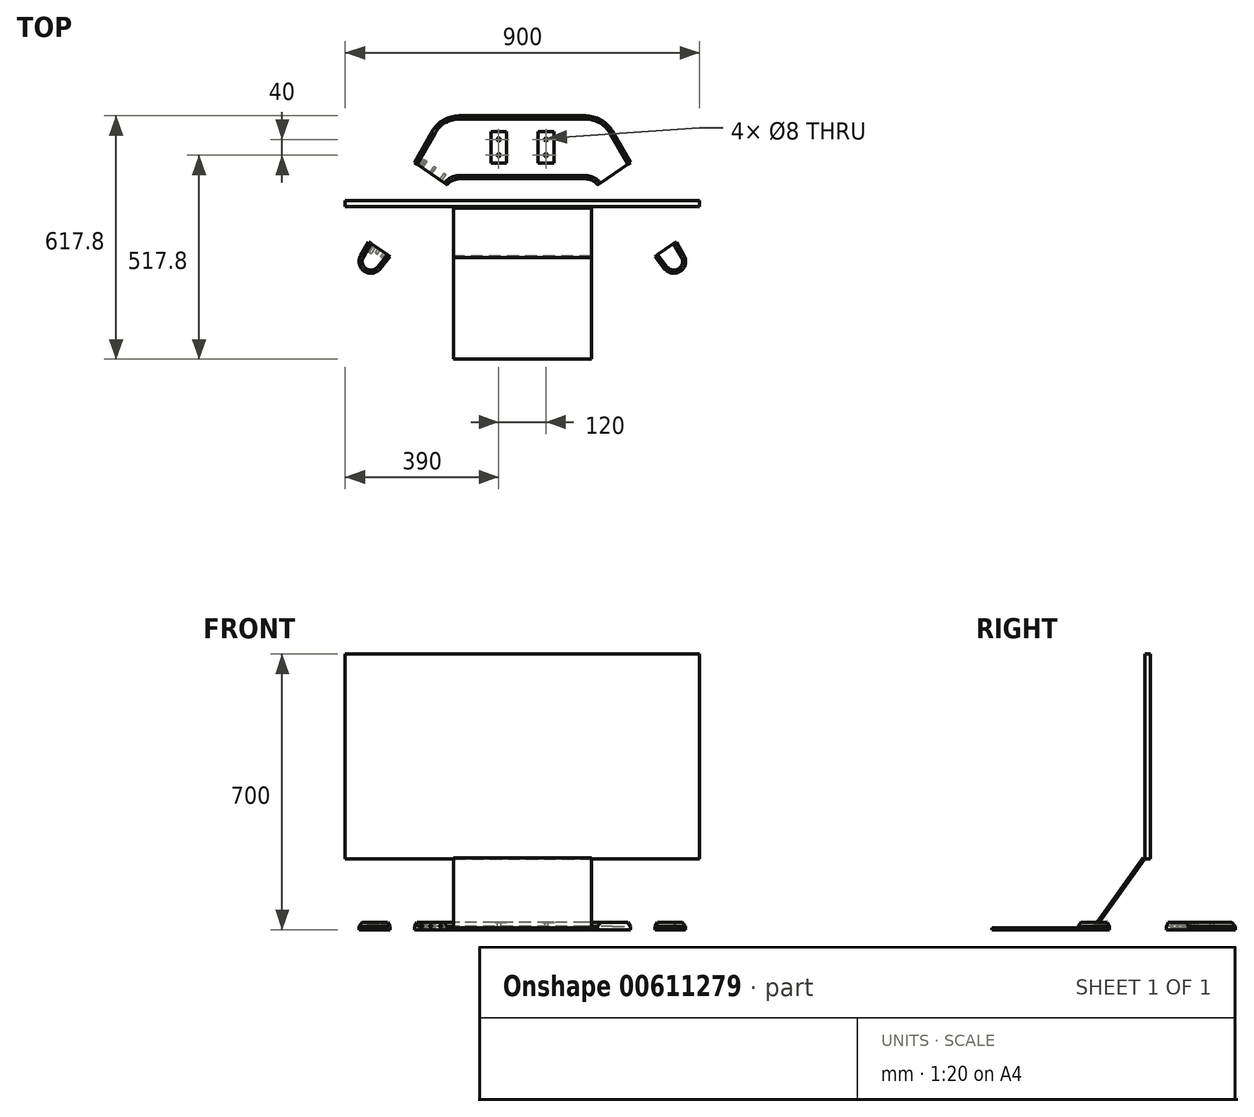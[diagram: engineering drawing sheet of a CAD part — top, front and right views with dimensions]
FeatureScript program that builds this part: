
annotation { "Feature Type Name" : "Feature", "Feature Type Description" : "" }
export const myFeature = defineFeature(function(context is Context, id is Id, definition is map)
    precondition{}
    {
        {
            var Q0;
            Q0=qCreatedBy(makeId("Right.planeOp"),FACE);
            var sketch = newSketch(context, id + "F0", { "sketchPlane" : qUnion([Q0])});
            skLineSegment(sketch, "E0", {"start": v(-150, 180) * mm, "end": v(-150, 700) * mm});
            skLineSegment(sketch, "E1.bottom", {"start": v(-280, 0) * mm, "end": v(-537.8, 0) * mm});
            skLineSegment(sketch, "E1.top", {"start": v(-280, 5) * mm, "end": v(-537.8, 5) * mm});
            skLineSegment(sketch, "E1.left", {"start": v(-280, 0) * mm, "end": v(-280, 5) * mm});
            skLineSegment(sketch, "E1.right", {"start": v(-537.8, 0) * mm, "end": v(-537.8, 5) * mm});
            skLineSegment(sketch, "E2", {"start": v(-280, 5) * mm, "end": v(-275.92, 2.11) * mm});
            skLineSegment(sketch, "E3", {"start": v(-275.92, 2.11) * mm, "end": v(-150, 180) * mm});
            skLineSegment(sketch, "E4", {"start": v(-150, 180) * mm, "end": v(-154.08, 182.89) * mm});
            skLineSegment(sketch, "E5", {"start": v(-154.08, 182.89) * mm, "end": v(-280, 5) * mm});
            skSolve(sketch);
        }
        {
            var Q0;
            Q0=sQuery(id+"F0.wireOp",EDGE,"E0");
            extrude(context, id + "F1", {"bodyType" : ToolBodyType.SURFACE, "surfaceEntities" : qUnion([Q0]), "endBound" : BoundingType.SYMMETRIC, "depth" : 900 * mm, "offsetDistance" : 25 * mm});
        }
        {
            var Q0;
            Q0=makeQuery(id+"F1.opExtrude","SWEPT_FACE",FACE,{"disambiguationData":[OSD([sQuery(id+"F0.wireOp",EDGE,"E0")])]});
            var Q1;
            Q1 = qSketchRegion(id + "FAVnxSPwo9muXU8_0", true);
            extrude(context, id + "F2", {"entities" : qUnion([Q0, Q1]), "depth" : 15 * mm, "offsetDistance" : 25 * mm});
        }
        {
            var Q0;
            Q0=makeQuery(id+"F0.imprint","IMPRINT",FACE,{"disambiguationData":[TD([[makeQuery(id+"F0.imprint","IMPRINT",EDGE,{"derivedFrom":sQuery(id+"F0.wireOp",EDGE,"E2")}),1.0]])]});
            var Q1;
            Q1=makeQuery(id+"F0.imprint","IMPRINT",FACE,{"disambiguationData":[TD([[makeQuery(id+"F0.imprint","IMPRINT",EDGE,{"derivedFrom":sQuery(id+"F0.wireOp",EDGE,"E1.bottom")}),-1.0]])]});
            extrude(context, id + "F3", {"entities" : qUnion([Q0, Q1]), "endBound" : BoundingType.SYMMETRIC, "depth" : 350 * mm, "offsetDistance" : 25 * mm});
        }
        {
            var Q0;
            Q0=qCreatedBy(makeId("Top.planeOp"),FACE);
            var sketch = newSketch(context, id + "F4", { "sketchPlane" : qUnion([Q0])});
            skLineSegment(sketch, "E6.bottom", {"start": v(-40, -40) * mm, "end": v(-80, -40) * mm});
            skLineSegment(sketch, "E6.top", {"start": v(-40, 40) * mm, "end": v(-80, 40) * mm});
            skLineSegment(sketch, "E6.left", {"start": v(-40, -40) * mm, "end": v(-40, 40) * mm});
            skLineSegment(sketch, "E6.right", {"start": v(-80, -40) * mm, "end": v(-80, 40) * mm});
            skPoint(sketch, "E6.middle", {"position": v(-60, 0) * mm});
            skCircle(sketch, "E7", {"center": v(-60, 20) * mm, "radius": 4 * mm});
            skCircle(sketch, "E8", {"center": v(-60, -20) * mm, "radius": 4 * mm});
            skLineSegment(sketch, "E9.bottom", {"start": v(80, -40) * mm, "end": v(40, -40) * mm});
            skLineSegment(sketch, "E9.top", {"start": v(80, 40) * mm, "end": v(40, 40) * mm});
            skLineSegment(sketch, "E9.left", {"start": v(80, -40) * mm, "end": v(80, 40) * mm});
            skLineSegment(sketch, "E9.right", {"start": v(40, -40) * mm, "end": v(40, 40) * mm});
            skPoint(sketch, "E9.middle", {"position": v(60, 0) * mm});
            skCircle(sketch, "E10", {"center": v(60, 20) * mm, "radius": 4 * mm});
            skCircle(sketch, "E11", {"center": v(60, -20) * mm, "radius": 4 * mm});
            skLineSegment(sketch, "E12.bottom", {"start": v(-160, 80) * mm, "end": v(160, 80) * mm});
            skLineSegment(sketch, "E12.top", {"start": v(-160, -80) * mm, "end": v(160, -80) * mm});
            skLineSegment(sketch, "E12.left", {"start": v(-160, 80) * mm, "end": v(-160, -80) * mm});
            skLineSegment(sketch, "E12.right", {"start": v(160, 80) * mm, "end": v(160, -80) * mm});
            skPoint(sketch, "E13", {"position": v(-211.4, -380) * mm});
            skArc(sketch, "E14", {"start": v(-160, 80) * mm, "mid": v(-200.01, 69.27) * mm, "end": v(-229.3, 39.97) * mm});
            skArc(sketch, "E15", {"start": v(-410.99, -275.01) * mm, "mid": v(-401.9, -314.8) * mm, "end": v(-361.54, -308.7) * mm});
            skLineSegment(sketch, "E16", {"start": v(-229.3, 39.97) * mm, "end": v(-410.99, -275.01) * mm});
            skArc(sketch, "E17", {"start": v(-160, -80) * mm, "mid": v(-177.36, -83.96) * mm, "end": v(-191.28, -95.07) * mm});
            skLineSegment(sketch, "E18", {"start": v(-361.54, -308.7) * mm, "end": v(-191.28, -95.07) * mm});
            skArc(sketch, "E19", {"start": v(229.3, 39.97) * mm, "mid": v(200.01, 69.27) * mm, "end": v(160, 80) * mm});
            skArc(sketch, "E20", {"start": v(191.28, -95.07) * mm, "mid": v(177.36, -83.96) * mm, "end": v(160, -80) * mm});
            skArc(sketch, "E21", {"start": v(361.54, -308.7) * mm, "mid": v(401.9, -314.8) * mm, "end": v(410.99, -275.01) * mm});
            skLineSegment(sketch, "E22", {"start": v(191.28, -95.07) * mm, "end": v(361.54, -308.7) * mm});
            skLineSegment(sketch, "E23", {"start": v(229.3, 39.97) * mm, "end": v(410.99, -275.01) * mm});
            skLineSegment(sketch, "E24", {"start": v(-570.65, -290) * mm, "end": v(713.46, -290) * mm, "construction": true});
            skLineSegment(sketch, "E25", {"start": v(0, 249.14) * mm, "end": v(0, -674.1) * mm, "construction": true});
            skLineSegment(sketch, "E26", {"start": v(-390.94, -240.26) * mm, "end": v(-336.54, -277.33) * mm});
            skLineSegment(sketch, "E27", {"start": v(-191.28, -95.07) * mm, "end": v(-274.5, -38.38) * mm});
            skLineSegment(sketch, "E28", {"start": v(-410.99, -275.01) * mm, "end": v(-361.54, -308.7) * mm, "construction": true});
            skLineSegment(sketch, "E29.MirrorCS", {"start": v(191.28, -95.07) * mm, "end": v(274.5, -38.38) * mm});
            skLineSegment(sketch, "E30.MirrorCS", {"start": v(390.94, -240.26) * mm, "end": v(336.54, -277.33) * mm});
            skLineSegment(sketch, "E31", {"start": v(-391.27, -255.77) * mm, "end": v(-350.18, -283.77) * mm});
            skLineSegment(sketch, "E32", {"start": v(-350.18, -283.77) * mm, "end": v(-354.55, -289.26) * mm});
            skLineSegment(sketch, "E33", {"start": v(-354.55, -289.26) * mm, "end": v(-394.78, -261.85) * mm});
            skLineSegment(sketch, "E34", {"start": v(-394.78, -261.85) * mm, "end": v(-391.27, -255.77) * mm});
            skSolve(sketch);
        }
        {
            var Q0;
            Q0=makeQuery(id+"F4.imprint","IMPRINT",FACE,{"disambiguationData":[TD([[makeQuery(id+"F4.imprint","IMPRINT",EDGE,{"derivedFrom":sQuery(id+"F4.wireOp",EDGE,"E6.bottom")}),1.0]])]});
            extrude(context, id + "F5", {"entities" : qUnion([Q0]), "depth" : 18 * mm, "offsetDistance" : 25 * mm});
        }
        {
            var Q0;
            Q0=makeQuery(id+"F4.imprint","IMPRINT",FACE,{"disambiguationData":[TD([[makeQuery(id+"F4.imprint","IMPRINT",EDGE,{"derivedFrom":sQuery(id+"F4.wireOp",EDGE,"E12.right")}),1.0]])]});
            var Q1;
            Q1=makeQuery(id+"F4.imprint","IMPRINT",FACE,{"disambiguationData":[TD([[makeQuery(id+"F4.imprint","IMPRINT",EDGE,{"derivedFrom":sQuery(id+"F4.wireOp",EDGE,"E12.left")}),-1.0]])]});
            var Q2;
            {var subQ0=sQuery(id+"F4.wireOp",EDGE,"E15");Q2=makeQuery(id+"F4.imprint","IMPRINT",FACE,{"disambiguationData":[TD([[makeQuery(id+"F4.imprint","IMPRINT",EDGE,{"derivedFrom":subQ0}),1.0]])]});}
            var Q3;
            {var subQ0=sQuery(id+"F4.wireOp",EDGE,"E21");Q3=makeQuery(id+"F4.imprint","IMPRINT",FACE,{"disambiguationData":[TD([[makeQuery(id+"F4.imprint","IMPRINT",EDGE,{"derivedFrom":subQ0}),1.0]])]});}
            var Q4;
            Q4=makeQuery(id+"F4.imprint","IMPRINT",FACE,{"disambiguationData":[TD([[makeQuery(id+"F4.imprint","IMPRINT",EDGE,{"derivedFrom":sQuery(id+"F4.wireOp",EDGE,"E31")}),-1.0]])]});
            extrude(context, id + "F6", {"entities" : qUnion([Q0, Q1, Q2, Q3, Q4]), "operationType" : NewBodyOperationType.ADD, "depth" : 18 * mm, "offsetDistance" : 25 * mm});
        }
        {
            var Q0;
            Q0=makeQuery(id+"F4.imprint","IMPRINT",FACE,{"disambiguationData":[TD([[makeQuery(id+"F4.imprint","IMPRINT",EDGE,{"derivedFrom":sQuery(id+"F4.wireOp",EDGE,"E6.bottom")}),-1.0]])]});
            var Q1;
            Q1=makeQuery(id+"F4.imprint","IMPRINT",FACE,{"disambiguationData":[TD([[makeQuery(id+"F4.imprint","IMPRINT",EDGE,{"derivedFrom":sQuery(id+"F4.wireOp",EDGE,"E9.bottom")}),-1.0]])]});
            extrude(context, id + "F7", {"entities" : qUnion([Q0, Q1]), "operationType" : NewBodyOperationType.ADD, "depth" : 17 * mm, "offsetDistance" : 25 * mm});
        }
        {
            var Q0;
            Q0=makeQuery(id+"F5.opExtrude","CAP_EDGE",EDGE,{"disambiguationData":[OSD([sQuery(id+"F4.wireOp",EDGE,"E12.top")])],"isStart":false});
            var Q1;
            {var subQ0=sQuery(id+"F4.wireOp",EDGE,"E16");Q1=makeQuery(id+"F6.opExtrude","CAP_EDGE",EDGE,{"disambiguationData":[OSD([subQ0]),TDD([makeQuery(id+"F4.imprint","IMPRINT",EDGE,{"disambiguationData":[TD([[makeQuery(id+"F4.imprint","INTERSECT",VERTEX,{"derivedFrom":[sQuery(id+"F4.wireOp",EDGE,"E14"),subQ0]}),-1.0]])],"derivedFrom":subQ0})])],"isStart":false});}
            var Q2;
            {var subQ0=sQuery(id+"F4.wireOp",EDGE,"E16");Q2=makeQuery(id+"F6.opExtrude","CAP_EDGE",EDGE,{"disambiguationData":[OSD([subQ0]),TDD([makeQuery(id+"F4.imprint","IMPRINT",EDGE,{"disambiguationData":[TD([[makeQuery(id+"F4.imprint","INTERSECT",VERTEX,{"derivedFrom":[sQuery(id+"F4.wireOp",EDGE,"E15"),subQ0]}),1.0]])],"derivedFrom":subQ0})])],"isStart":false});}
            var Q3;
            Q3=makeQuery(id+"F6.opExtrude","CAP_EDGE",EDGE,{"disambiguationData":[OSD([sQuery(id+"F4.wireOp",EDGE,"E22")])],"isStart":false});
            chamfer(context, id + "F8", {"entities" : qUnion([Q0, Q1, Q2, Q3]), "chamferType" : ChamferType.TWO_OFFSETS, "width1" : 8 * mm, "oppositeDirection" : false, "width2" : 10 * mm, "tangentPropagation" : true});
        }
        {
            var Q0;
            Q0=makeQuery(id+"F6.opExtrude","SWEPT_FACE",FACE,{"disambiguationData":[OSD([sQuery(id+"F4.wireOp",EDGE,"E27")])]});
            var sketch = newSketch(context, id + "F9", { "sketchPlane" : qUnion([Q0])});
            skLineSegment(sketch, "E35", {"start": v(-112.57, 18) * mm, "end": v(-197.22, 18) * mm, "construction": true});
            skCircle(sketch, "E36", {"center": v(-154.9, 9) * mm, "radius": 4 * mm});
            skLineSegment(sketch, "E37", {"start": v(-204.44, 9) * mm, "end": v(-105.36, 9) * mm});
            skCircle(sketch, "E38", {"center": v(-184.9, 9) * mm, "radius": 4 * mm});
            skCircle(sketch, "E39.MirrorC", {"center": v(-124.9, 9.78) * mm, "radius": 4 * mm});
            skLineSegment(sketch, "E40", {"start": v(-154.9, 0) * mm, "end": v(-154.9, 9) * mm, "construction": true});
            skLineSegment(sketch, "E41", {"start": v(-154.9, 9) * mm, "end": v(-154.9, 18) * mm, "construction": true});
            skSolve(sketch);
        }
        {
            var Q0;
            Q0=makeQuery(id+"F6.opExtrude","SWEPT_FACE",FACE,{"disambiguationData":[OSD([sQuery(id+"F4.wireOp",EDGE,"E26")])]});
            var sketch = newSketch(context, id + "F10", { "sketchPlane" : qUnion([Q0])});
            skLineSegment(sketch, "E42", {"start": v(179.8, 18) * mm, "end": v(130, 18) * mm, "construction": true});
            skLineSegment(sketch, "E43", {"start": v(154.9, 18) * mm, "end": v(154.9, 9) * mm, "construction": true});
            skPoint(sketch, "E43.startSnap0", {"position": v(154.9, 18) * mm});
            skLineSegment(sketch, "E44", {"start": v(122.78, 9) * mm, "end": v(187.01, 9) * mm, "construction": true});
            skCircle(sketch, "E45", {"center": v(137.9, 9) * mm, "radius": 3 * mm});
            skCircle(sketch, "E46.MirrorC", {"center": v(171.9, 9) * mm, "radius": 3 * mm});
            skCircle(sketch, "E47.cCircle", {"center": v(137.9, 9) * mm, "radius": 5.5 * mm, "construction": true});
            skLineSegment(sketch, "E47.0", {"start": v(143.4, 12.18) * mm, "end": v(143.4, 5.82) * mm});
            skLineSegment(sketch, "E47.1", {"start": v(143.4, 5.82) * mm, "end": v(137.9, 2.65) * mm});
            skLineSegment(sketch, "E47.2", {"start": v(137.9, 2.65) * mm, "end": v(132.4, 5.82) * mm});
            skLineSegment(sketch, "E47.3", {"start": v(132.4, 5.82) * mm, "end": v(132.4, 12.18) * mm});
            skLineSegment(sketch, "E47.4", {"start": v(132.4, 12.18) * mm, "end": v(137.9, 15.35) * mm});
            skLineSegment(sketch, "E47.5", {"start": v(137.9, 15.35) * mm, "end": v(143.4, 12.18) * mm});
            skPoint(sketch, "E47.0.midPoint", {"position": v(143.4, 9) * mm});
            skLineSegment(sketch, "E48", {"start": v(154.9, 9) * mm, "end": v(154.9, 0) * mm, "construction": true});
            skCircle(sketch, "E49", {"center": v(154.9, 9) * mm, "radius": 3 * mm});
            skLineSegment(sketch, "E50.MirrorCS", {"start": v(166.4, 5.82) * mm, "end": v(171.9, 2.65) * mm});
            skLineSegment(sketch, "E51.MirrorCS", {"start": v(171.9, 15.35) * mm, "end": v(166.4, 12.18) * mm});
            skLineSegment(sketch, "E52.MirrorCS", {"start": v(177.4, 12.18) * mm, "end": v(171.9, 15.35) * mm});
            skLineSegment(sketch, "E53.MirrorCS", {"start": v(177.4, 5.82) * mm, "end": v(177.4, 12.18) * mm});
            skLineSegment(sketch, "E54.MirrorCS", {"start": v(166.4, 12.18) * mm, "end": v(166.4, 5.82) * mm});
            skLineSegment(sketch, "E55.MirrorCS", {"start": v(171.9, 2.65) * mm, "end": v(177.4, 5.82) * mm});
            skCircle(sketch, "E56.cCircle", {"center": v(154.9, 9) * mm, "radius": 5.5 * mm, "construction": true});
            skLineSegment(sketch, "E56.0", {"start": v(160.4, 12.18) * mm, "end": v(160.4, 5.82) * mm});
            skLineSegment(sketch, "E56.1", {"start": v(160.4, 5.82) * mm, "end": v(154.9, 2.65) * mm});
            skLineSegment(sketch, "E56.2", {"start": v(154.9, 2.65) * mm, "end": v(149.4, 5.82) * mm});
            skLineSegment(sketch, "E56.3", {"start": v(149.4, 5.82) * mm, "end": v(149.4, 12.18) * mm});
            skLineSegment(sketch, "E56.4", {"start": v(149.4, 12.18) * mm, "end": v(154.9, 15.35) * mm});
            skLineSegment(sketch, "E56.5", {"start": v(154.9, 15.35) * mm, "end": v(160.4, 12.18) * mm});
            skPoint(sketch, "E56.0.midPoint", {"position": v(160.4, 9) * mm});
            skLineSegment(sketch, "E57", {"start": v(132.4, 5.82) * mm, "end": v(132.4, 0) * mm});
            skLineSegment(sketch, "E58", {"start": v(143.4, 5.82) * mm, "end": v(143.4, 0) * mm});
            skLineSegment(sketch, "E59", {"start": v(143.4, 0) * mm, "end": v(132.4, 0) * mm});
            skLineSegment(sketch, "E60", {"start": v(149.4, 5.82) * mm, "end": v(149.4, 0) * mm});
            skLineSegment(sketch, "E61", {"start": v(160.4, 5.82) * mm, "end": v(160.4, 0) * mm});
            skLineSegment(sketch, "E62", {"start": v(160.4, 0) * mm, "end": v(149.4, 0) * mm});
            skLineSegment(sketch, "E63", {"start": v(177.4, 5.82) * mm, "end": v(177.4, 0) * mm});
            skLineSegment(sketch, "E64", {"start": v(166.4, 5.82) * mm, "end": v(166.4, 0) * mm});
            skLineSegment(sketch, "E65", {"start": v(166.4, 0) * mm, "end": v(177.4, 0) * mm});
            skSolve(sketch);
        }
        {
            var Q0;
            Q0=sQuery(id+"F9.wireOp",EDGE,"E37");
            extrude(context, id + "F11", {"bodyType" : ToolBodyType.SURFACE, "surfaceEntities" : qUnion([Q0]), "depth" : 260 * mm, "offsetDistance" : 25 * mm, "hasSecondDirection" : true, "secondDirectionOppositeDirection" : true, "secondDirectionDepth" : 25 * mm});
        }
        {
            var Q0;
            Q0=makeQuery(id+"F11.opExtrude","SWEPT_FACE",FACE,{"disambiguationData":[OSD([sQuery(id+"F9.wireOp",EDGE,"E37")])]});
            var sketch = newSketch(context, id + "F12", { "sketchPlane" : qUnion([Q0])});
            skLineSegment(sketch, "E66", {"start": v(-257.68, 49.83) * mm, "end": v(-377.8, 249.23) * mm});
            skLineSegment(sketch, "E67", {"start": v(-232.89, 66.72) * mm, "end": v(-363.74, 258.8) * mm});
            skLineSegment(sketch, "E68", {"start": v(-208.1, 83.62) * mm, "end": v(-349.7, 268.37) * mm});
            skLineSegment(sketch, "E69", {"start": v(-377.8, 249.23) * mm, "end": v(-384.5, 260.36) * mm});
            skLineSegment(sketch, "E70", {"start": v(-363.74, 258.8) * mm, "end": v(-371.06, 269.54) * mm});
            skLineSegment(sketch, "E71", {"start": v(-349.7, 268.37) * mm, "end": v(-357.6, 278.69) * mm});
            skLineSegment(sketch, "E72", {"start": v(-257.68, 49.83) * mm, "end": v(-247.37, 32.71) * mm});
            skLineSegment(sketch, "E73", {"start": v(-232.89, 66.72) * mm, "end": v(-221.63, 50.2) * mm});
            skLineSegment(sketch, "E74", {"start": v(-208.1, 83.62) * mm, "end": v(-196.84, 67.1) * mm});
            skLineSegment(sketch, "E75", {"start": v(-384.5, 260.36) * mm, "end": v(-388.11, 266.36) * mm});
            skLineSegment(sketch, "E76", {"start": v(-371.06, 269.54) * mm, "end": v(-375, 275.33) * mm});
            skLineSegment(sketch, "E77", {"start": v(-357.6, 278.69) * mm, "end": v(-361.86, 284.24) * mm});
            skSolve(sketch);
        }
        {
            var Q0;
            Q0=makeQuery(id+"F10.imprint","IMPRINT",FACE,{"disambiguationData":[TD([[makeQuery(id+"F10.imprint","IMPRINT",EDGE,{"derivedFrom":sQuery(id+"F10.wireOp",EDGE,"E49")}),1.0]])]});
            var Q1;
            Q1=sQuery(id+"F12.wireOp",EDGE,"E67");
            var Q2;
            Q2=sQuery(id+"F12.wireOp",EDGE,"E73");
            var Q3;
            Q3=sQuery(id+"F12.wireOp",EDGE,"E70");
            sweep(context, id + "F13", {"operationType" : NewBodyOperationType.REMOVE, "profiles" : qUnion([Q0]), "path" : qUnion([Q1, Q2, Q3])});
        }
        {
            var Q0;
            Q0=makeQuery(id+"F10.imprint","IMPRINT",FACE,{"disambiguationData":[TD([[makeQuery(id+"F10.imprint","IMPRINT",EDGE,{"derivedFrom":sQuery(id+"F10.wireOp",EDGE,"E46.MirrorC")}),-1.0]])]});
            var Q1;
            Q1=sQuery(id+"F12.wireOp",EDGE,"E72");
            var Q2;
            Q2=sQuery(id+"F12.wireOp",EDGE,"E66");
            var Q3;
            Q3=sQuery(id+"F12.wireOp",EDGE,"E69");
            var Q4;
            Q4=sQuery(id+"F12.wireOp",EDGE,"E75");
            sweep(context, id + "F14", {"operationType" : NewBodyOperationType.REMOVE, "profiles" : qUnion([Q0]), "path" : qUnion([Q1, Q2, Q3, Q4])});
        }
        {
            var Q0;
            Q0=makeQuery(id+"F10.imprint","IMPRINT",FACE,{"disambiguationData":[TD([[makeQuery(id+"F10.imprint","IMPRINT",EDGE,{"derivedFrom":sQuery(id+"F10.wireOp",EDGE,"E45")}),1.0]])]});
            var Q1;
            Q1=sQuery(id+"F12.wireOp",EDGE,"E74");
            var Q2;
            Q2=sQuery(id+"F12.wireOp",EDGE,"E68");
            var Q3;
            Q3=sQuery(id+"F12.wireOp",EDGE,"E71");
            sweep(context, id + "F15", {"operationType" : NewBodyOperationType.REMOVE, "profiles" : qUnion([Q0]), "path" : qUnion([Q1, Q2, Q3])});
        }
        {
            var Q0;
            Q0=makeQuery(id+"F10.imprint","IMPRINT",FACE,{"disambiguationData":[TD([[makeQuery(id+"F10.imprint","IMPRINT",EDGE,{"derivedFrom":sQuery(id+"F10.wireOp",EDGE,"E46.MirrorC")}),1.0]])]});
            var Q1;
            Q1=makeQuery(id+"F10.imprint","IMPRINT",FACE,{"disambiguationData":[TD([[makeQuery(id+"F10.imprint","IMPRINT",EDGE,{"derivedFrom":sQuery(id+"F10.wireOp",EDGE,"E50.MirrorCS")}),-1.0]])]});
            var Q2;
            Q2=sQuery(id+"F10.wireOp",EDGE,"E64");
            var Q3;
            Q3=sQuery(id+"F10.wireOp",EDGE,"E54.MirrorCS");
            var Q4;
            Q4=sQuery(id+"F10.wireOp",EDGE,"E51.MirrorCS");
            var Q5;
            Q5=sQuery(id+"F10.wireOp",EDGE,"E52.MirrorCS");
            var Q6;
            Q6=sQuery(id+"F10.wireOp",EDGE,"E53.MirrorCS");
            var Q7;
            Q7=sQuery(id+"F10.wireOp",EDGE,"E63");
            var Q8;
            Q8=sQuery(id+"F10.wireOp",EDGE,"E65");
            var Q9;
            Q9=sQuery(id+"F12.wireOp",EDGE,"E69");
            var Q10;
            Q10=sQuery(id+"F12.wireOp",EDGE,"E75");
            sweep(context, id + "F16", {"operationType" : NewBodyOperationType.REMOVE, "profiles" : qUnion([Q0, Q1]), "surfaceProfiles" : qUnion([Q2, Q3, Q4, Q5, Q6, Q7, Q8]), "path" : qUnion([Q9, Q10])});
        }
    });
